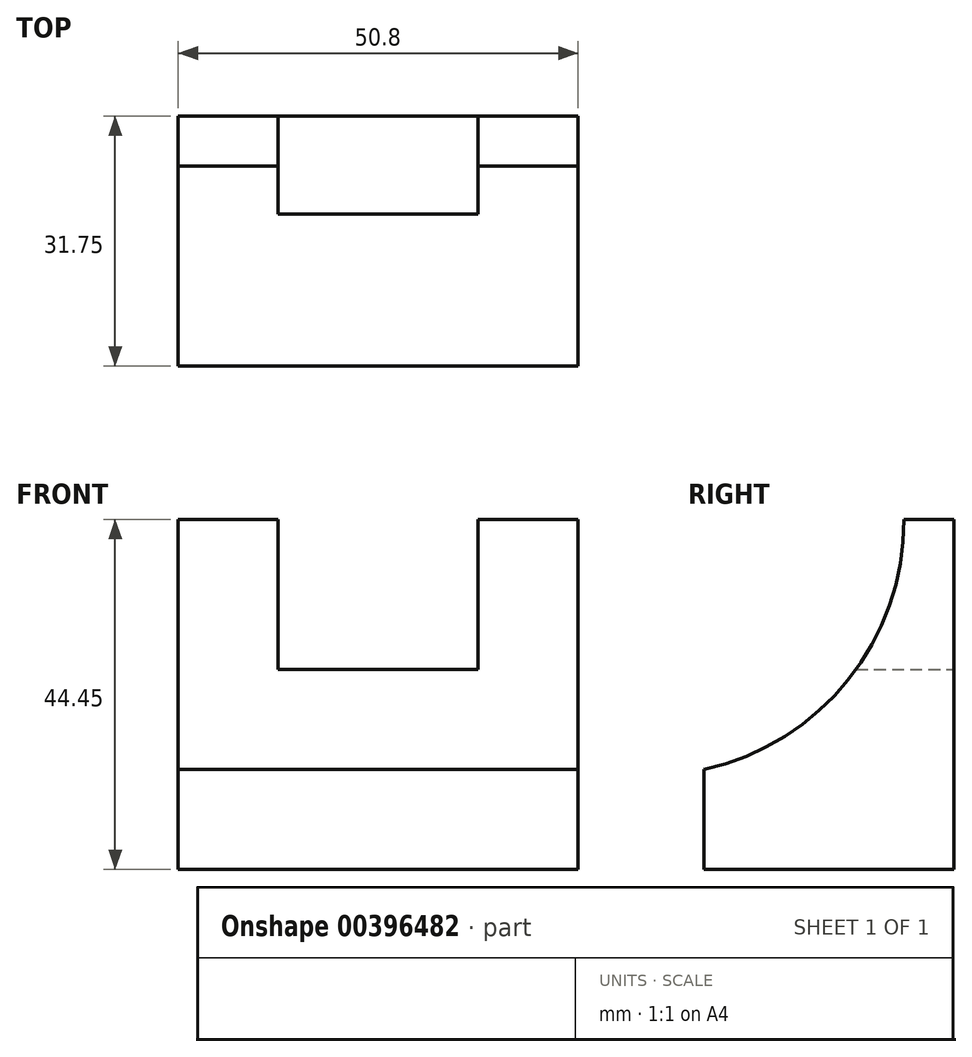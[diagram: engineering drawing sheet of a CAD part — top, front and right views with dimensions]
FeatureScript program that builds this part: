
annotation { "Feature Type Name" : "Feature", "Feature Type Description" : "" }
export const myFeature = defineFeature(function(context is Context, id is Id, definition is map)
    precondition{}
    {
        {
            var Q0;
            Q0=qCreatedBy(makeId("Front.planeOp"),FACE);
            var sketch = newSketch(context, id + "F0", { "sketchPlane" : qUnion([Q0])});
            skLineSegment(sketch, "E0", {"start": v(0, 0) * mm, "end": v(0, 44.45) * mm});
            skLineSegment(sketch, "E1", {"start": v(0, 44.45) * mm, "end": v(50.8, 44.45) * mm});
            skLineSegment(sketch, "E2", {"start": v(50.8, 44.45) * mm, "end": v(50.8, 0) * mm});
            skLineSegment(sketch, "E3", {"start": v(50.8, 0) * mm, "end": v(0, 0) * mm});
            skSolve(sketch);
        }
        {
            var Q0;
            Q0=makeQuery(id+"F0.imprint","IMPRINT",FACE,{"disambiguationData":[TD([[makeQuery(id+"F0.imprint","IMPRINT",EDGE,{"derivedFrom":sQuery(id+"F0.wireOp",EDGE,"E0")}),-1.0]])]});
            extrude(context, id + "F1", {"entities" : qUnion([Q0]), "depth" : 31.75 * mm});
        }
        {
            var Q0;
            Q0=makeQuery(id+"F1.opExtrude","SWEPT_FACE",FACE,{"disambiguationData":[OSD([sQuery(id+"F0.wireOp",EDGE,"E2")])]});
            var sketch = newSketch(context, id + "F2", { "sketchPlane" : qUnion([Q0])});
            skArc(sketch, "E4", {"start": v(-31.75, 12.7) * mm, "mid": v(-13.44, 24.1) * mm, "end": v(-6.35, 44.45) * mm});
            skLineSegment(sketch, "E5", {"start": v(-6.35, 44.45) * mm, "end": v(0, 44.45) * mm});
            skLineSegment(sketch, "E6", {"start": v(0, 44.45) * mm, "end": v(0, 0) * mm});
            skLineSegment(sketch, "E7", {"start": v(0, 0) * mm, "end": v(-31.75, 0) * mm});
            skLineSegment(sketch, "E8", {"start": v(-31.75, 0) * mm, "end": v(-31.75, 12.7) * mm});
            skSolve(sketch);
        }
        {
            var Q0;
            {var subQ0=sQuery(id+"F2.wireOp",EDGE,"E4");Q0=makeQuery(id+"F2.imprint","IMPRINT",FACE,{"disambiguationData":[TD([[makeQuery(id+"F2.imprint","IMPRINT",EDGE,{"derivedFrom":subQ0}),1.0]])]});}
            extrude(context, id + "F3", {"entities" : qUnion([Q0]), "operationType" : NewBodyOperationType.REMOVE, "oppositeDirection" : true, "depth" : 76.2 * mm});
        }
        {
            var Q0;
            Q0=makeQuery(id+"F1.opExtrude","CAP_FACE",FACE,{"disambiguationData":[OSD([sQuery(id+"F0.wireOp",EDGE,"E0"),sQuery(id+"F0.wireOp",EDGE,"E1"),sQuery(id+"F0.wireOp",EDGE,"E2"),sQuery(id+"F0.wireOp",EDGE,"E3")])],"isStart":true});
            var sketch = newSketch(context, id + "F4", { "sketchPlane" : qUnion([Q0])});
            skLineSegment(sketch, "E9", {"start": v(-38.1, 44.45) * mm, "end": v(-38.1, 25.4) * mm});
            skLineSegment(sketch, "E10", {"start": v(-38.1, 25.4) * mm, "end": v(-12.7, 25.4) * mm});
            skLineSegment(sketch, "E11", {"start": v(-12.7, 25.4) * mm, "end": v(-12.7, 44.45) * mm});
            skLineSegment(sketch, "E12", {"start": v(-12.7, 44.45) * mm, "end": v(-38.1, 44.45) * mm});
            skSolve(sketch);
        }
        {
            var Q0;
            Q0=makeQuery(id+"F4.imprint","IMPRINT",FACE,{"disambiguationData":[TD([[makeQuery(id+"F4.imprint","IMPRINT",EDGE,{"derivedFrom":sQuery(id+"F4.wireOp",EDGE,"E9")}),1.0]])]});
            extrude(context, id + "F5", {"entities" : qUnion([Q0]), "operationType" : NewBodyOperationType.REMOVE, "oppositeDirection" : true, "depth" : 25.4 * mm});
        }
    });
